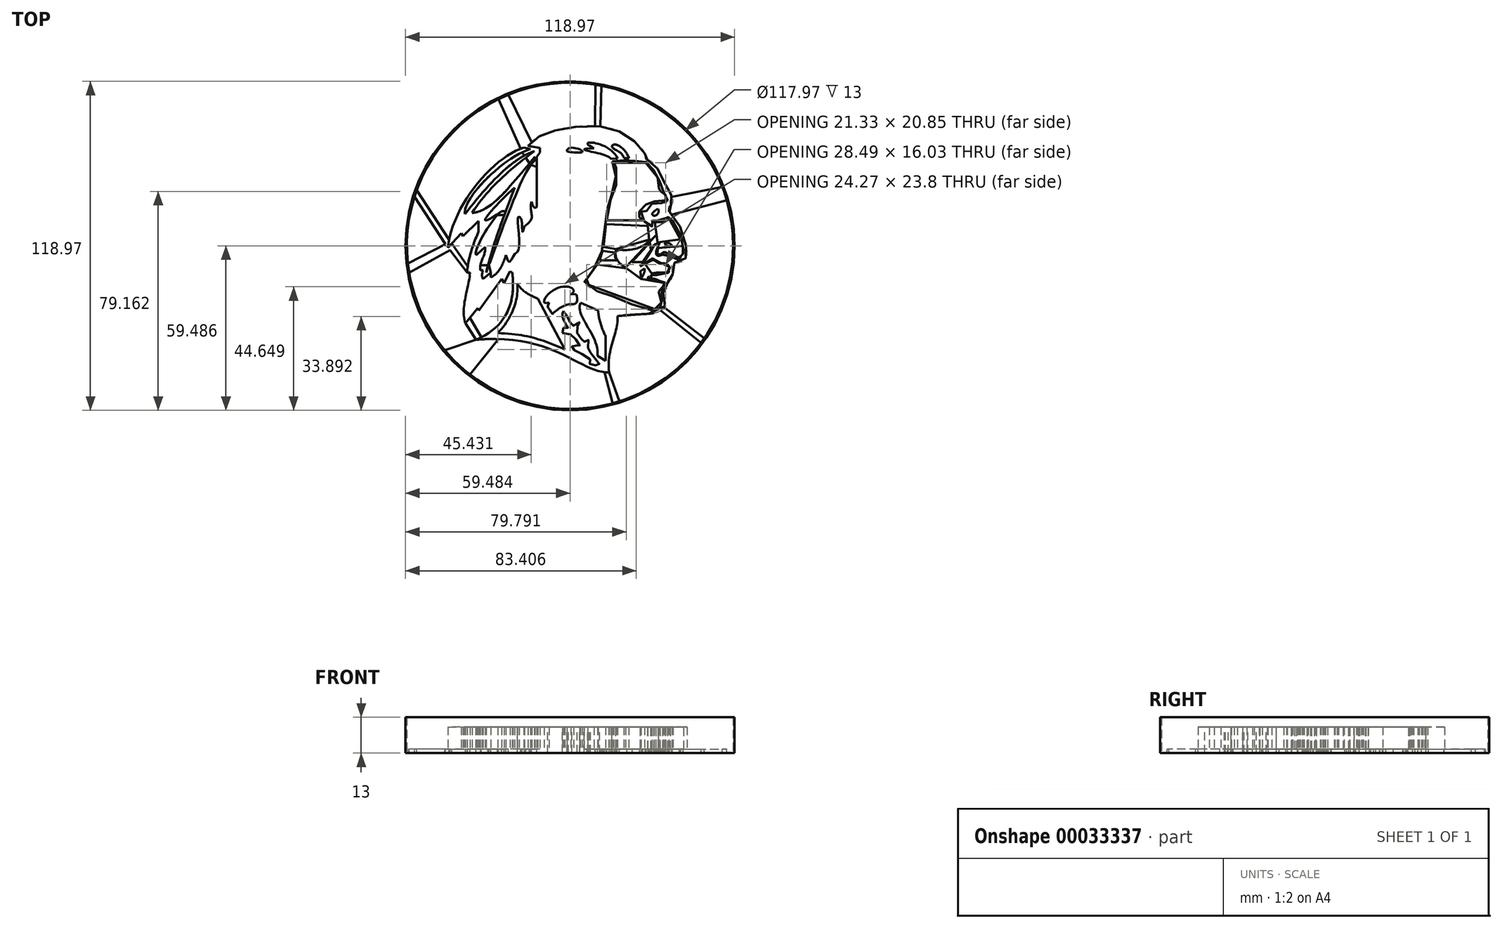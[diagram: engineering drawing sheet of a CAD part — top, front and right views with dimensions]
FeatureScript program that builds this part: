
annotation { "Feature Type Name" : "Feature", "Feature Type Description" : "" }
export const myFeature = defineFeature(function(context is Context, id is Id, definition is map)
    precondition{}
    {
        {
            var Q0;
            Q0=qCreatedBy(makeId("Top.planeOp"),FACE);
            var sketch = newSketch(context, id + "F0", { "sketchPlane" : qUnion([Q0])});
            skCircle(sketch, "E0", {"center": v(7.53, 11.46) * mm, "radius": 59.49 * mm});
            skPoint(sketch, "E0.first.point", {"position": v(-51.93, 13.03) * mm});
            skPoint(sketch, "E0.second.point", {"position": v(66.92, 7.92) * mm});
            skPoint(sketch, "E0.third.point", {"position": v(5.79, 70.92) * mm});
            skSolve(sketch);
        }
        {
            var Q0;
            Q0=makeQuery(id+"F0.imprint","IMPRINT",FACE,{"disambiguationData":[TD([[makeQuery(id+"F0.imprint","IMPRINT",EDGE,{"derivedFrom":sQuery(id+"F0.wireOp",EDGE,"E0")}),1.0]])]});
            extrude(context, id + "F1", {"entities" : qUnion([Q0]), "depth" : 12 * mm});
        }
        {
            var Q0;
            Q0=makeQuery(id+"F1.opExtrude","CAP_FACE",FACE,{"disambiguationData":[OSD([sQuery(id+"F0.wireOp",EDGE,"E0")])],"isStart":false});
            shell(context, id + "F2", {"entities" : qUnion([Q0]), "thickness" : .5 * mm});
        }
        {
            var Q0;
            {var subQ0=sQuery(id+"F0.wireOp",EDGE,"E0");Q0=makeQuery(id+"F2.opShell","OFFSET_FACE",FACE,{"disambiguationData":[OSD([subQ0]),TDD([makeQuery(id+"F1.opExtrude","CAP_FACE",FACE,{"disambiguationData":[OSD([subQ0])],"isStart":true})])]});}
            var sketch = newSketch(context, id + "F3", { "sketchPlane" : qUnion([Q0])});
            skFitSpline(sketch, "E1", {"points": [v(-9.15, 46.95) * mm, v(-36.63, 10.74) * mm], "startDerivative": vector(-33.15, -9.52) * mm, "endDerivative": vector(-3.72, -44.42) * mm});
            skFitSpline(sketch, "E2", {"points": [v(-36.63, 10.74) * mm, v(-31.8, 15.95) * mm], "startDerivative": vector(4.82, 5.2) * mm, "endDerivative": vector(4.82, 5.2) * mm});
            skFitSpline(sketch, "E3", {"points": [v(-31.8, 15.95) * mm, v(-31.11, 14.95) * mm], "startDerivative": vector(0.69, -1) * mm, "endDerivative": vector(0.69, -1) * mm});
            skFitSpline(sketch, "E4", {"points": [v(-5.09, 42.36) * mm, v(-5.09, 43.66) * mm], "startDerivative": vector(0, 1.3) * mm, "endDerivative": vector(0, 1.3) * mm});
            skFitSpline(sketch, "E5", {"points": [v(-5.09, 43.66) * mm, v(-27.88, 23.37) * mm], "startDerivative": vector(-23.04, -26.12) * mm, "endDerivative": vector(-22.32, -0.88) * mm});
            skFitSpline(sketch, "E6", {"points": [v(-27.88, 23.37) * mm, v(-5.34, 45.7) * mm], "startDerivative": vector(17.84, 27.64) * mm, "endDerivative": vector(23.73, 17.5) * mm});
            skFitSpline(sketch, "E7", {"points": [v(-5.34, 45.7) * mm, v(-30.47, 22.94) * mm], "startDerivative": vector(-25.9, -8.68) * mm, "endDerivative": vector(-24.74, -31.1) * mm});
            skFitSpline(sketch, "E8", {"points": [v(-30.47, 22.94) * mm, v(-6.79, 46.48) * mm], "startDerivative": vector(-3.33, 15.62) * mm, "endDerivative": vector(31.1, 9.84) * mm});
            skFitSpline(sketch, "E9", {"points": [v(-6.79, 46.48) * mm, v(-9.15, 46.95) * mm], "startDerivative": vector(-2.36, 0.47) * mm, "endDerivative": vector(-2.36, 0.47) * mm});
            skFitSpline(sketch, "E10", {"points": [v(-31.11, 14.95) * mm, v(-25.52, 20.45) * mm], "startDerivative": vector(5.6, 5.5) * mm, "endDerivative": vector(5.6, 5.5) * mm});
            skFitSpline(sketch, "E11", {"points": [v(-25.52, 20.45) * mm, v(-25.52, 16.55) * mm], "startDerivative": vector(0, -3.9) * mm, "endDerivative": vector(0, -3.9) * mm});
            skFitSpline(sketch, "E12", {"points": [v(-25.52, 16.55) * mm, v(-29.7, 1.74) * mm], "startDerivative": vector(-6.96, -15.11) * mm, "endDerivative": vector(-0.88, -13.52) * mm});
            skFitSpline(sketch, "E13", {"points": [v(-29.7, 1.74) * mm, v(-28.61, 1.74) * mm], "startDerivative": vector(1.09, 0) * mm, "endDerivative": vector(1.09, 0) * mm});
            skFitSpline(sketch, "E14", {"points": [v(-28.61, 1.74) * mm, v(-30.24, -16.6) * mm], "startDerivative": vector(-1.62, -18.33) * mm, "endDerivative": vector(6.1, -16.78) * mm});
            skFitSpline(sketch, "E15", {"points": [v(-30.24, -16.6) * mm, v(-25.84, -11.03) * mm], "startDerivative": vector(4.4, 5.57) * mm, "endDerivative": vector(4.4, 5.57) * mm});
            skFitSpline(sketch, "E16", {"points": [v(-25.84, -11.03) * mm, v(-25.44, -12) * mm], "startDerivative": vector(0.4, -0.96) * mm, "endDerivative": vector(0.4, -0.96) * mm});
            skFitSpline(sketch, "E17", {"points": [v(-25.44, -12) * mm, v(-17.17, -0.55) * mm], "startDerivative": vector(8.27, 11.44) * mm, "endDerivative": vector(8.27, 11.44) * mm});
            skFitSpline(sketch, "E18", {"points": [v(-17.17, -0.55) * mm, v(-16.27, -1.99) * mm], "startDerivative": vector(0.9, -1.44) * mm, "endDerivative": vector(0.9, -1.44) * mm});
            skFitSpline(sketch, "E19", {"points": [v(-16.27, -1.99) * mm, v(-14.18, 2.32) * mm], "startDerivative": vector(2.1, 4.3) * mm, "endDerivative": vector(2.1, 4.3) * mm});
            skFitSpline(sketch, "E20", {"points": [v(-14.18, 2.32) * mm, v(-13.39, 1.7) * mm], "startDerivative": vector(0.8, -0.62) * mm, "endDerivative": vector(0.8, -0.62) * mm});
            skFitSpline(sketch, "E21", {"points": [v(-13.39, 1.7) * mm, v(-26.5, -22.52) * mm], "startDerivative": vector(3.2, -23.1) * mm, "endDerivative": vector(-39.4, -16.16) * mm});
            skFitSpline(sketch, "E22", {"points": [v(-26.5, -22.52) * mm, v(21.64, -34.31) * mm], "startDerivative": vector(86.82, 7.34) * mm, "endDerivative": vector(31.4, 1.39) * mm});
            skFitSpline(sketch, "E23", {"points": [v(21.64, -34.31) * mm, v(24.69, -14) * mm], "startDerivative": vector(-2.89, 25.9) * mm, "endDerivative": vector(-2.05, 15.2) * mm});
            skFitSpline(sketch, "E24", {"points": [v(24.69, -14) * mm, v(39.93, -12.2) * mm, v(42.05, -8.84) * mm, v(41.21, -5.53) * mm, v(42.66, -3.65) * mm, v(43.16, -0.9) * mm, v(44.42, -0.49) * mm, v(44.42, 5.18) * mm, v(45.19, 5.3) * mm, v(48.22, 5.86) * mm, v(49.79, 8.1) * mm, v(49.5, 11.54) * mm, v(46.75, 19.39) * mm, v(43.4, 23.85) * mm, v(43.33, 24.4) * mm, v(43.73, 26.1) * mm, v(44.36, 26.48) * mm, v(44.66, 28.5) * mm, v(42.08, 33.4) * mm, v(40.66, 36.42) * mm, v(38.63, 40.1) * mm, v(35.68, 42.55) * mm, v(35.22, 42.59) * mm, v(35.02, 43.17) * mm, v(34.4, 45.2) * mm, v(31.33, 48.76) * mm, v(26.07, 52.42) * mm, v(18.52, 54.63) * mm, v(7.38, 54.25) * mm, v(0.41, 52.69) * mm, v(-4.75, 50.41) * mm, v(-7.71, 47.66) * mm], "startDerivative": vector(305.64, 45.18) * mm, "endDerivative": vector(-76.3, -84.2) * mm});
            skFitSpline(sketch, "E25", {"points": [v(-7.71, 47.66) * mm, v(-3.36, 46.9) * mm], "startDerivative": vector(4.35, -0.77) * mm, "endDerivative": vector(4.35, -0.77) * mm});
            skFitSpline(sketch, "E26", {"points": [v(-3.36, 46.9) * mm, v(-3.36, 45.21) * mm], "startDerivative": vector(0, -1.68) * mm, "endDerivative": vector(0, -1.68) * mm});
            skFitSpline(sketch, "E27", {"points": [v(-3.36, 45.21) * mm, v(-4.46, 43.68) * mm], "startDerivative": vector(-1.1, -1.53) * mm, "endDerivative": vector(-1.1, -1.53) * mm});
            skFitSpline(sketch, "E28", {"points": [v(-4.46, 43.68) * mm, v(-4.46, 25.48) * mm], "startDerivative": vector(0, -18.2) * mm, "endDerivative": vector(0, -18.2) * mm});
            skFitSpline(sketch, "E29", {"points": [v(-4.46, 25.48) * mm, v(-6.37, 27.36) * mm], "startDerivative": vector(-2.7, -1.39) * mm, "endDerivative": vector(-1.92, 7.05) * mm});
            skFitSpline(sketch, "E30", {"points": [v(-6.37, 27.36) * mm, v(-6.37, 21.44) * mm, v(-8.9, 18.53) * mm], "startDerivative": vector(-4.08, -13.4) * mm, "endDerivative": vector(-6.92, -5.6) * mm});
            skFitSpline(sketch, "E31", {"points": [v(-8.9, 18.53) * mm, v(-9.67, 16.48) * mm, v(-10.03, 20.82) * mm, v(-11, 21.93) * mm, v(-11.43, 20.6) * mm, v(-10.99, 10.19) * mm, v(-12.7, 8.17) * mm, v(-14.41, 5.61) * mm, v(-15.63, 8.07) * mm], "startDerivative": vector(-9.44, -31.77) * mm, "endDerivative": vector(-9.92, 32.78) * mm});
            skFitSpline(sketch, "E32", {"points": [v(-15.63, 8.07) * mm, v(-21.11, 0) * mm], "startDerivative": vector(-3.75, -12.02) * mm, "endDerivative": vector(-7.77, -3.86) * mm});
            skFitSpline(sketch, "E33", {"points": [v(-21.11, 0) * mm, v(-21.11, 1.8) * mm], "startDerivative": vector(0, 1.8) * mm, "endDerivative": vector(0, 1.8) * mm});
            skFitSpline(sketch, "E34", {"points": [v(-21.11, 1.8) * mm, v(-23.96, -0.53) * mm], "startDerivative": vector(-2.85, -2.33) * mm, "endDerivative": vector(-2.85, -2.33) * mm});
            skFitSpline(sketch, "E35", {"points": [v(-23.96, -0.53) * mm, v(-23.96, 2.67) * mm], "startDerivative": vector(-1.2, 1.6) * mm, "endDerivative": vector(1.41, 4.07) * mm});
            skFitSpline(sketch, "E36", {"points": [v(-23.96, 2.67) * mm, v(-24.9, 2.67) * mm], "startDerivative": vector(-0.94, 0) * mm, "endDerivative": vector(-0.94, 0) * mm});
            skFitSpline(sketch, "E37", {"points": [v(-24.9, 2.67) * mm, v(-23.15, 11.01) * mm], "startDerivative": vector(-1.4, 8.6) * mm, "endDerivative": vector(-1.04, 8.36) * mm});
            skFitSpline(sketch, "E38", {"points": [v(-23.15, 11.01) * mm, v(-26.14, 8.3) * mm], "startDerivative": vector(-3, -2.7) * mm, "endDerivative": vector(-3, -2.7) * mm});
            skFitSpline(sketch, "E39", {"points": [v(-26.14, 8.3) * mm, v(-17.24, 24) * mm], "startDerivative": vector(-6.04, -1.8) * mm, "endDerivative": vector(16.01, 13.76) * mm});
            skFitSpline(sketch, "E40", {"points": [v(-17.24, 24) * mm, v(-12.45, 32.51) * mm], "startDerivative": vector(-44.66, -32.02) * mm, "endDerivative": vector(6.2, 4.22) * mm});
            skFitSpline(sketch, "E41", {"points": [v(-12.45, 32.51) * mm, v(-22.84, 1.74) * mm], "startDerivative": vector(-12.12, -31.5) * mm, "endDerivative": vector(-7.38, -30.43) * mm});
            skFitSpline(sketch, "E42", {"points": [v(-22.84, 1.74) * mm, v(-5.09, 42.36) * mm], "startDerivative": vector(16.99, 44.79) * mm, "endDerivative": vector(12.56, 7.44) * mm});
            skFitSpline(sketch, "E43", {"points": [v(12.05, 45.52) * mm, v(7.29, 45.42) * mm, v(6.43, 45.97) * mm, v(8.14, 46.93) * mm, v(12.05, 45.52) * mm]});
            skFitSpline(sketch, "E44", {"points": [v(16.2, 46.76) * mm, v(22.31, 42.96) * mm], "startDerivative": vector(-30.9, -1.52) * mm, "endDerivative": vector(4.22, -7.27) * mm});
            skFitSpline(sketch, "E45", {"points": [v(27, 43.12) * mm, v(28.81, 43.11) * mm], "startDerivative": vector(1.8, 0) * mm, "endDerivative": vector(1.8, 0) * mm});
            skFitSpline(sketch, "E46", {"points": [v(28.81, 43.11) * mm, v(23.37, 48.1) * mm], "startDerivative": vector(-1.96, 7.28) * mm, "endDerivative": vector(-5.93, -0.5) * mm});
            skFitSpline(sketch, "E47", {"points": [v(23.37, 48.1) * mm, v(27, 43.12) * mm], "startDerivative": vector(-8.2, -4.56) * mm, "endDerivative": vector(1.09, -9.1) * mm});
            skFitSpline(sketch, "E48", {"points": [v(22.77, 42) * mm, v(24.02, 38.9) * mm, v(23, 30.55) * mm, v(22.05, 28.83) * mm, v(20.78, 23.25) * mm, v(19.76, 14.45) * mm, v(17.96, 6.24) * mm, v(14.46, 1.05) * mm, v(12.8, -1.85) * mm, v(16.95, -4.86) * mm, v(22.21, -6.53) * mm, v(27.8, -8.95) * mm, v(36.7, -11.8) * mm, v(38.2, -11.94) * mm, v(39.57, -11.43) * mm, v(40.86, -10.04) * mm, v(40.9, -7.95) * mm, v(40.26, -5.58) * mm, v(40.28, -5.02) * mm, v(41.6, -3.23) * mm, v(42.08, -1.93) * mm, v(41.24, -1.74) * mm, v(37.72, -0.43) * mm, v(35.64, -0.43) * mm, v(35.72, 0) * mm, v(37.52, 1.28) * mm, v(37.92, 1.44) * mm, v(38.3, 1.19) * mm, v(38.9, 0.82) * mm, v(40.5, 1.38) * mm, v(43.37, 1.72) * mm, v(43.83, 2.46) * mm, v(43.67, 3.48) * mm, v(42.02, 5.29) * mm, v(39.93, 5.31) * mm, v(37.95, 6.65) * mm, v(37.48, 6.85) * mm, v(37.08, 6.7) * mm, v(32.87, 4.05) * mm], "startDerivative": vector(53.72, -79.37) * mm, "endDerivative": vector(-145.32, -92.55) * mm});
            skFitSpline(sketch, "E49", {"points": [v(32.87, 4.05) * mm, v(37.87, 11.85) * mm], "startDerivative": vector(6.86, 7.68) * mm, "endDerivative": vector(2.48, 7.9) * mm});
            skFitSpline(sketch, "E50", {"points": [v(37.87, 11.85) * mm, v(39.97, 12.6) * mm], "startDerivative": vector(2.17, 0.47) * mm, "endDerivative": vector(2.1, 0.75) * mm});
            skFitSpline(sketch, "E51", {"points": [v(39.97, 12.6) * mm, v(41.1, 8.23) * mm], "startDerivative": vector(-3.77, -8.3) * mm, "endDerivative": vector(11.52, 4.15) * mm});
            skFitSpline(sketch, "E52", {"points": [v(41.1, 8.23) * mm, v(41.86, 8.62) * mm, v(42.96, 8.23) * mm, v(44.51, 7.28) * mm, v(45.65, 6.6) * mm, v(46.69, 6.46) * mm, v(47.87, 7.03) * mm, v(48.63, 8.23) * mm, v(48.52, 10.96) * mm, v(47.22, 16.12) * mm, v(44.96, 20.18) * mm, v(43.24, 21.99) * mm, v(42.96, 22.17) * mm, v(42.6, 21.75) * mm, v(41.44, 20.79) * mm, v(39.83, 20.61) * mm, v(39.44, 20.67) * mm, v(39.6, 20.22) * mm, v(37.61, 20.59) * mm, v(37.3, 20.55) * mm, v(37.31, 20.21) * mm, v(37.82, 19.5) * mm, v(37.8, 19) * mm, v(36.65, 18.25) * mm, v(36.09, 18.45) * mm, v(34.51, 20.12) * mm, v(33.03, 22.68) * mm, v(33.08, 23.53) * mm, v(33.76, 24.06) * mm, v(34.4, 24.16) * mm, v(34.68, 23.83) * mm, v(35.35, 24.16) * mm, v(36.07, 25.01) * mm, v(36.7, 25.45) * mm, v(36.68, 25.61) * mm, v(35.87, 25.8) * mm, v(35.9, 26.22) * mm, v(36.75, 26.32) * mm, v(37.2, 26.6) * mm, v(38.58, 27.25) * mm, v(40.25, 27.04) * mm, v(41.4, 26.62) * mm, v(42.43, 26.85) * mm, v(42.85, 27.98) * mm, v(42.8, 29.21) * mm, v(41.7, 30.82) * mm, v(40.53, 31.68) * mm, v(39.96, 34.35) * mm, v(39.26, 36.62) * mm, v(37.44, 39.18) * mm, v(36.38, 40.67) * mm, v(34.92, 41.78) * mm, v(32.2, 41.95) * mm, v(31.04, 42.13) * mm, v(29.01, 42.2) * mm, v(27.4, 42.37) * mm, v(25.34, 42.35) * mm, v(22.77, 42) * mm], "startDerivative": vector(51.42, 38.87) * mm, "endDerivative": vector(-106.33, -16.92) * mm});
            skFitSpline(sketch, "E53", {"points": [v(16.2, 46.76) * mm, v(24.71, 43.06) * mm], "startDerivative": vector(-22.76, 10.16) * mm, "endDerivative": vector(8.73, -19.57) * mm});
            skFitSpline(sketch, "E54", {"points": [v(24.71, 43.06) * mm, v(22.31, 42.96) * mm], "startDerivative": vector(-2.4, -0.1) * mm, "endDerivative": vector(-2.4, -0.1) * mm});
            skFitSpline(sketch, "E55", {"points": [v(38.58, 15.26) * mm, v(24.23, 10.1) * mm], "startDerivative": vector(-13.9, -13.92) * mm, "endDerivative": vector(-19.24, 2.1) * mm});
            skFitSpline(sketch, "E56", {"points": [v(24.23, 10.1) * mm, v(27.6, 3.65) * mm], "startDerivative": vector(-3.71, -11.3) * mm, "endDerivative": vector(2.74, -1.3) * mm});
            skFitSpline(sketch, "E57", {"points": [v(27.6, 3.65) * mm, v(38.58, 15.26) * mm], "startDerivative": vector(10.98, 11.6) * mm, "endDerivative": vector(10.98, 11.6) * mm});
            skFitSpline(sketch, "E58", {"points": [v(34.44, 3.25) * mm, v(32.92, 2.22) * mm], "startDerivative": vector(-1.52, -1.03) * mm, "endDerivative": vector(-1.52, -1.03) * mm});
            skFitSpline(sketch, "E59", {"points": [v(32.92, 2.22) * mm, v(33.18, -0.23) * mm], "startDerivative": vector(0.25, -2.44) * mm, "endDerivative": vector(0.25, -2.44) * mm});
            skFitSpline(sketch, "E60", {"points": [v(33.18, -0.23) * mm, v(34.44, 3.25) * mm], "startDerivative": vector(2.3, 2.04) * mm, "endDerivative": vector(-0.83, 3.64) * mm});
            skFitSpline(sketch, "E61", {"points": [v(41.6, 12.58) * mm, v(42.8, 11.4) * mm, v(44.44, 11.52) * mm], "startDerivative": vector(2.14, -3) * mm, "endDerivative": vector(3.52, 0.88) * mm});
            skFitSpline(sketch, "E62", {"points": [v(44.44, 11.52) * mm, v(41.6, 12.58) * mm], "startDerivative": vector(-0.58, 1.08) * mm, "endDerivative": vector(-4.54, -0.7) * mm});
            skFitSpline(sketch, "E63", {"points": [v(39.34, 24.81) * mm, v(37.18, 23.06) * mm], "startDerivative": vector(-2.94, -1.27) * mm, "endDerivative": vector(-1.66, -1.96) * mm});
            skFitSpline(sketch, "E64", {"points": [v(37.18, 23.06) * mm, v(37.95, 22.27) * mm, v(39.52, 23.42) * mm, v(39.34, 24.81) * mm], "startDerivative": vector(2.06, -4) * mm, "endDerivative": vector(-1.81, 4.2) * mm});
            skFitSpline(sketch, "E65", {"points": [v(5.62, -26.04) * mm, v(-4.17, -7.65) * mm], "startDerivative": vector(-9.78, 18.39) * mm, "endDerivative": vector(-9.78, 18.39) * mm});
            skFitSpline(sketch, "E66", {"points": [v(-4.17, -7.65) * mm, v(-11.58, -2.24) * mm], "startDerivative": vector(-6.61, 3.26) * mm, "endDerivative": vector(-7.29, 10.64) * mm});
            skFitSpline(sketch, "E67", {"points": [v(-11.58, -2.24) * mm, v(-18.65, -20.12) * mm], "startDerivative": vector(2.01, -15.17) * mm, "endDerivative": vector(-16.38, -16.45) * mm});
            skFitSpline(sketch, "E68", {"points": [v(-18.65, -20.12) * mm, v(5.62, -26.04) * mm], "startDerivative": vector(31.26, -0.68) * mm, "endDerivative": vector(22.67, -10.11) * mm});
            skFitSpline(sketch, "E69", {"points": [v(11.35, -9.15) * mm, v(17.73, -11.9) * mm], "startDerivative": vector(6.38, -2.76) * mm, "endDerivative": vector(6.38, -2.76) * mm});
            skFitSpline(sketch, "E70", {"points": [v(17.73, -11.9) * mm, v(20.35, -21.18) * mm], "startDerivative": vector(0.1, -9.8) * mm, "endDerivative": vector(3.25, -6.64) * mm});
            skFitSpline(sketch, "E71", {"points": [v(20.35, -21.18) * mm, v(20.35, -30.17) * mm], "startDerivative": vector(0, -9) * mm, "endDerivative": vector(0, -9) * mm});
            skFitSpline(sketch, "E72", {"points": [v(20.35, -30.17) * mm, v(17.48, -28.39) * mm], "startDerivative": vector(-2.87, 1.78) * mm, "endDerivative": vector(-2.87, 1.78) * mm});
            skFitSpline(sketch, "E73", {"points": [v(17.48, -28.39) * mm, v(11.35, -9.15) * mm], "startDerivative": vector(2.06, 23.36) * mm, "endDerivative": vector(6.67, 14.81) * mm});
            skFitSpline(sketch, "E74", {"points": [v(0, -9.06) * mm, v(3.2, -3.73) * mm, v(7.87, -6.13) * mm], "startDerivative": vector(-23.87, -7.6) * mm, "endDerivative": vector(-17.62, -12.06) * mm});
            skFitSpline(sketch, "E75", {"points": [v(0, -9.06) * mm, v(-0.5, -10.53) * mm, v(0, -11.45) * mm, v(0.95, -13) * mm, v(1.2, -13.24) * mm, v(1.46, -12.93) * mm, v(4.94, -10.46) * mm, v(7.65, -9.67) * mm, v(9.2, -9.62) * mm, v(10, -8.8) * mm, v(10.13, -7.42) * mm, v(9.76, -6.2) * mm, v(7.87, -6.13) * mm], "startDerivative": vector(-9.3, -18.83) * mm, "endDerivative": vector(-24.1, -3.27) * mm});
            skFitSpline(sketch, "E76", {"points": [v(5.15, -12.23) * mm, v(4.8, -14.56) * mm], "startDerivative": vector(-1.66, -2.16) * mm, "endDerivative": vector(-0.35, -2.33) * mm});
            skLineSegment(sketch, "E77", {"start": v(5.16, -18.17) * mm, "end": v(4.8, -20.08) * mm});
            skFitSpline(sketch, "E78", {"points": [v(4.8, -14.56) * mm, v(6.58, -17.76) * mm, v(6.86, -18.15) * mm, v(6.47, -18.22) * mm, v(5.16, -18.17) * mm], "startDerivative": vector(4.5, -9.02) * mm, "endDerivative": vector(-5.43, 0.3) * mm});
            skFitSpline(sketch, "E79", {"points": [v(4.8, -20.08) * mm, v(7.4, -20.5) * mm, v(8.48, -21.14) * mm, v(9.97, -22.86) * mm, v(11, -24.44) * mm, v(11.03, -24.72) * mm, v(10.18, -24.78) * mm, v(9.44, -24.53) * mm, v(8.32, -24.54) * mm, v(8.25, -25.12) * mm, v(8.52, -26.11) * mm, v(9.1, -26.3) * mm, v(11.26, -27.24) * mm, v(14.56, -29.5) * mm, v(14.87, -29.8) * mm, v(14.9, -30.32) * mm, v(14.69, -31.58) * mm, v(14.88, -31.82) * mm, v(17.89, -31.75) * mm, v(18.22, -31.67) * mm, v(18.05, -31.1) * mm, v(14.09, -26.14) * mm, v(13.93, -25.9) * mm, v(14.03, -25.38) * mm, v(14.16, -22.84) * mm, v(14.03, -22.42) * mm, v(13.67, -22.58) * mm, v(12.5, -23.32) * mm, v(12.2, -23.18) * mm, v(11.71, -22.31) * mm, v(10.36, -20.87) * mm, v(10.06, -19.29) * mm, v(10.28, -17.57) * mm, v(10.98, -16.7) * mm, v(11, -16.27) * mm, v(10.42, -16.38) * mm, v(8.46, -17.57) * mm, v(8, -17.62) * mm, v(7.23, -15.48) * mm, v(6.46, -14.04) * mm, v(6.43, -13.4) * mm, v(5.15, -12.23) * mm], "startDerivative": vector(79.68, -9.23) * mm, "endDerivative": vector(-58.5, 41.16) * mm});
            skSolve(sketch);
        }
        {
            var Q0;
            Q0=makeQuery(id+"F3.imprint","IMPRINT",FACE,{"disambiguationData":[TD([[makeQuery(id+"F3.imprint","IMPRINT",EDGE,{"derivedFrom":sQuery(id+"F3.wireOp",EDGE,"E1")}),1.0]])]});
            var Q1;
            Q1=makeQuery(id+"F3.imprint","IMPRINT",FACE,{"disambiguationData":[TD([[makeQuery(id+"F3.imprint","IMPRINT",EDGE,{"derivedFrom":sQuery(id+"F3.wireOp",EDGE,"E55")}),1.0]])]});
            var Q2;
            Q2=makeQuery(id+"F3.imprint","IMPRINT",FACE,{"disambiguationData":[TD([[makeQuery(id+"F3.imprint","IMPRINT",EDGE,{"derivedFrom":sQuery(id+"F3.wireOp",EDGE,"E61")}),1.0]])]});
            extrude(context, id + "F4", {"entities" : qUnion([Q0, Q1, Q2]), "operationType" : NewBodyOperationType.ADD, "depth" : 8 * mm});
        }
        {
            var Q0;
            Q0=makeQuery(id+"F1.opExtrude","CAP_FACE",FACE,{"disambiguationData":[OSD([sQuery(id+"F0.wireOp",EDGE,"E0")])],"isStart":true});
            extrude(context, id + "F5", {"entities" : qUnion([Q0]), "operationType" : NewBodyOperationType.ADD, "depth" : 1 * mm});
        }
        {
            var Q0;
            {var subQ0=sQuery(id+"F0.wireOp",EDGE,"E0");Q0=makeQuery(id+"F4.boolean.opBoolean","SPLIT",FACE,{"disambiguationData":[TD([makeQuery(id+"F4.opExtrude","SWEPT_FACE",FACE,{"disambiguationData":[OSD([sQuery(id+"F3.wireOp",EDGE,"E1")])]})])],"derivedFrom":makeQuery(id+"F2.opShell","OFFSET_FACE",FACE,{"disambiguationData":[OSD([subQ0]),TDD([makeQuery(id+"F1.opExtrude","CAP_FACE",FACE,{"disambiguationData":[OSD([subQ0])],"isStart":true})])]})});}
            var sketch = newSketch(context, id + "F6", { "sketchPlane" : qUnion([Q0])});
            skLineSegment(sketch, "E80", {"start": v(-18.36, -22.27) * mm, "end": v(-28.64, -35.13) * mm});
            skLineSegment(sketch, "E81", {"start": v(-26.5, -22.52) * mm, "end": v(-37.73, -26.37) * mm});
            skLineSegment(sketch, "E82", {"start": v(-30.24, -16.6) * mm, "end": v(-26.5, -22.52) * mm});
            skLineSegment(sketch, "E83", {"start": v(-28.66, -14.6) * mm, "end": v(-24.59, -21.65) * mm});
            skLineSegment(sketch, "E84", {"start": v(-36.63, 10.74) * mm, "end": v(-29.7, 1.74) * mm});
            skLineSegment(sketch, "E85", {"start": v(-35.24, 12.24) * mm, "end": v(-29.46, 3.99) * mm});
            skLineSegment(sketch, "E86", {"start": v(-36.63, 10.74) * mm, "end": v(-48.73, 29.18) * mm});
            skLineSegment(sketch, "E87", {"start": v(-36.2, 13.7) * mm, "end": v(-47.93, 31.55) * mm});
            skLineSegment(sketch, "E88", {"start": v(-35.92, 9.83) * mm, "end": v(-50.66, 1.8) * mm});
            skLineSegment(sketch, "E89", {"start": v(-37.51, 12.1) * mm, "end": v(-51.1, 5) * mm});
            skLineSegment(sketch, "E90", {"start": v(-51.1, 5) * mm, "end": v(-50.51, 5.07) * mm});
            skLineSegment(sketch, "E91", {"start": v(21.64, -34.31) * mm, "end": v(25.3, -44.8) * mm});
            skLineSegment(sketch, "E92", {"start": v(40.35, -11.97) * mm, "end": v(54.94, -23.65) * mm});
            skLineSegment(sketch, "E93", {"start": v(41.57, -10.78) * mm, "end": v(56.08, -22.05) * mm});
            skLineSegment(sketch, "E94", {"start": v(-22.15, 4.47) * mm, "end": v(-24.85, 4.47) * mm});
            skLineSegment(sketch, "E95", {"start": v(-21.82, 4.45) * mm, "end": v(-21.11, 1.8) * mm});
            skLineSegment(sketch, "E96", {"start": v(-18.76, 22.52) * mm, "end": v(-16.24, 22.52) * mm});
            skLineSegment(sketch, "E97", {"start": v(-17.24, 24) * mm, "end": v(-15.7, 24) * mm});
            skLineSegment(sketch, "E98", {"start": v(-4.46, 40.03) * mm, "end": v(-6.67, 40.73) * mm});
            skLineSegment(sketch, "E99", {"start": v(-7.13, 41.29) * mm, "end": v(-8.5, 43.32) * mm});
            skLineSegment(sketch, "E100", {"start": v(-8.91, 44.13) * mm, "end": v(-9.86, 45.23) * mm});
            skLineSegment(sketch, "E101", {"start": v(-9.15, 46.95) * mm, "end": v(-7.71, 47.66) * mm});
            skLineSegment(sketch, "E102", {"start": v(-10.4, 46.53) * mm, "end": v(-18.32, 64.47) * mm});
            skLineSegment(sketch, "E103", {"start": v(-6.44, 49) * mm, "end": v(-14.73, 66.08) * mm});
            skLineSegment(sketch, "E104", {"start": v(16.54, 54.78) * mm, "end": v(16.78, 69.71) * mm});
            skLineSegment(sketch, "E105", {"start": v(16.78, 69.71) * mm, "end": v(16.71, 69.23) * mm});
            skLineSegment(sketch, "E106", {"start": v(44.46, 29.17) * mm, "end": v(62.57, 32.68) * mm});
            skLineSegment(sketch, "E107", {"start": v(44.28, 22.72) * mm, "end": v(64.2, 27.85) * mm});
            skLineSegment(sketch, "E108", {"start": v(34.27, 4.94) * mm, "end": v(36.98, 1.01) * mm});
            skLineSegment(sketch, "E109", {"start": v(33.98, 5.26) * mm, "end": v(17.24, 6.03) * mm});
            skLineSegment(sketch, "E110", {"start": v(20.02, -34.26) * mm, "end": v(22.99, -45.47) * mm});
            skLineSegment(sketch, "E111", {"start": v(22.99, -45.47) * mm, "end": v(22.88, -45.13) * mm});
            skLineSegment(sketch, "E112", {"start": v(18.93, 70.54) * mm, "end": v(18.36, 52.47) * mm});
            skLineSegment(sketch, "E113", {"start": v(16.52, 4.82) * mm, "end": v(27.36, 4.35) * mm});
            skLineSegment(sketch, "E114", {"start": v(27.36, 4.35) * mm, "end": v(33.2, -0.21) * mm});
            skLineSegment(sketch, "E115", {"start": v(33.2, -0.21) * mm, "end": v(36.57, -0.21) * mm});
            skLineSegment(sketch, "E116", {"start": v(36.25, 19.55) * mm, "end": v(19.31, 19.55) * mm});
            skLineSegment(sketch, "E117", {"start": v(19.28, 20.44) * mm, "end": v(35.07, 20.44) * mm});
            skLineSegment(sketch, "E118", {"start": v(35.8, 19.16) * mm, "end": v(37.1, 8.64) * mm});
            skLineSegment(sketch, "E119", {"start": v(39.24, 11.64) * mm, "end": v(37.59, 19.3) * mm});
            skLineSegment(sketch, "E120", {"start": v(39.6, 12.47) * mm, "end": v(48.14, 13.55) * mm});
            skLineSegment(sketch, "E121", {"start": v(48.9, 11.54) * mm, "end": v(38.9, 10.97) * mm});
            skLineSegment(sketch, "E122", {"start": v(24.62, 8.8) * mm, "end": v(18.22, 10.12) * mm});
            skLineSegment(sketch, "E123", {"start": v(18.22, 10.12) * mm, "end": v(18.22, 11.08) * mm});
            skLineSegment(sketch, "E124", {"start": v(18.22, 11.08) * mm, "end": v(25.34, 9.62) * mm});
            skSolve(sketch);
        }
        {
            var Q0;
            {var subQ2=sQuery(id+"F6.wireOp",EDGE,"E87");Q0=makeQuery(id+"F6.imprint","IMPRINT",FACE,{"disambiguationData":[TD([[makeQuery(id+"F6.imprint","IMPRINT",EDGE,{"derivedFrom":subQ2}),-1.0]])]});}
            extrude(context, id + "F7", {"entities" : qUnion([Q0]), "operationType" : NewBodyOperationType.REMOVE, "oppositeDirection" : true, "depth" : 25 * mm});
        }
        {
            var Q0;
            {var subQ2=sQuery(id+"F6.wireOp",EDGE,"E103");Q0=makeQuery(id+"F6.imprint","IMPRINT",FACE,{"disambiguationData":[TD([[makeQuery(id+"F6.imprint","IMPRINT",EDGE,{"derivedFrom":subQ2}),-1.0]])]});}
            var Q1;
            {var subQ1=sQuery(id+"F6.wireOp",EDGE,"E100");Q1=makeQuery(id+"F6.imprint","IMPRINT",FACE,{"disambiguationData":[TD([[makeQuery(id+"F6.imprint","IMPRINT",EDGE,{"derivedFrom":subQ1}),1.0]])]});}
            var Q2;
            {var subQ1=sQuery(id+"F6.wireOp",EDGE,"E99");Q2=makeQuery(id+"F6.imprint","IMPRINT",FACE,{"disambiguationData":[TD([[makeQuery(id+"F6.imprint","IMPRINT",EDGE,{"derivedFrom":subQ1}),1.0]])]});}
            var Q3;
            {var subQ2=sQuery(id+"F6.wireOp",EDGE,"E95");Q3=makeQuery(id+"F6.imprint","IMPRINT",FACE,{"disambiguationData":[TD([[makeQuery(id+"F6.imprint","IMPRINT",EDGE,{"derivedFrom":subQ2}),1.0]])]});}
            var Q4;
            {var subQ1=sQuery(id+"F6.wireOp",EDGE,"E97");Q4=makeQuery(id+"F6.imprint","IMPRINT",FACE,{"disambiguationData":[TD([[makeQuery(id+"F6.imprint","IMPRINT",EDGE,{"derivedFrom":subQ1}),1.0]])]});}
            var Q5;
            {var subQ2=sQuery(id+"F6.wireOp",EDGE,"E94");Q5=makeQuery(id+"F6.imprint","IMPRINT",FACE,{"disambiguationData":[TD([[makeQuery(id+"F6.imprint","IMPRINT",EDGE,{"derivedFrom":subQ2}),-1.0]])]});}
            extrude(context, id + "F8", {"entities" : qUnion([Q0, Q1, Q2, Q3, Q4, Q5]), "operationType" : NewBodyOperationType.REMOVE, "oppositeDirection" : true, "depth" : 25 * mm});
        }
        {
            var Q0;
            {var subQ2=sQuery(id+"F6.wireOp",EDGE,"E93");Q0=makeQuery(id+"F6.imprint","IMPRINT",FACE,{"disambiguationData":[TD([[makeQuery(id+"F6.imprint","IMPRINT",EDGE,{"derivedFrom":subQ2}),1.0]])]});}
            var Q1;
            {var subQ5=sQuery(id+"F6.wireOp",EDGE,"E91");Q1=makeQuery(id+"F6.imprint","IMPRINT",FACE,{"disambiguationData":[TD([[makeQuery(id+"F6.imprint","IMPRINT",EDGE,{"derivedFrom":subQ5}),1.0]])]});}
            var Q2;
            {var subQ2=sQuery(id+"F6.wireOp",EDGE,"E80");Q2=makeQuery(id+"F6.imprint","IMPRINT",FACE,{"disambiguationData":[TD([[makeQuery(id+"F6.imprint","IMPRINT",EDGE,{"derivedFrom":subQ2}),1.0]])]});}
            var Q3;
            {var subQ1=sQuery(id+"F6.wireOp",EDGE,"E83");Q3=makeQuery(id+"F6.imprint","IMPRINT",FACE,{"disambiguationData":[TD([[makeQuery(id+"F6.imprint","IMPRINT",EDGE,{"derivedFrom":subQ1}),1.0]])]});}
            var Q4;
            {var subQ3=sQuery(id+"F6.wireOp",EDGE,"E81");Q4=makeQuery(id+"F6.imprint","IMPRINT",FACE,{"disambiguationData":[TD([[makeQuery(id+"F6.imprint","IMPRINT",EDGE,{"derivedFrom":subQ3}),-1.0]])]});}
            var Q5;
            {var subQ2=sQuery(id+"F6.wireOp",EDGE,"E89");Q5=makeQuery(id+"F6.imprint","IMPRINT",FACE,{"disambiguationData":[TD([[makeQuery(id+"F6.imprint","IMPRINT",EDGE,{"derivedFrom":subQ2}),-1.0]])]});}
            var Q6;
            {var subQ1=sQuery(id+"F6.wireOp",EDGE,"E85");Q6=makeQuery(id+"F6.imprint","IMPRINT",FACE,{"disambiguationData":[TD([[makeQuery(id+"F6.imprint","IMPRINT",EDGE,{"derivedFrom":subQ1}),1.0]])]});}
            extrude(context, id + "F9", {"entities" : qUnion([Q0, Q1, Q2, Q3, Q4, Q5, Q6]), "operationType" : NewBodyOperationType.REMOVE, "oppositeDirection" : true, "depth" : 25 * mm});
        }
        {
            var Q0;
            {var subQ3=sQuery(id+"F6.wireOp",EDGE,"E106");Q0=makeQuery(id+"F6.imprint","IMPRINT",FACE,{"disambiguationData":[TD([[makeQuery(id+"F6.imprint","IMPRINT",EDGE,{"derivedFrom":subQ3}),1.0]])]});}
            extrude(context, id + "F10", {"entities" : qUnion([Q0]), "operationType" : NewBodyOperationType.REMOVE, "oppositeDirection" : true, "depth" : 25 * mm});
        }
        {
            var Q0;
            Q0=makeQuery(id+"F3.imprint","IMPRINT",FACE,{"disambiguationData":[TD([[makeQuery(id+"F3.imprint","IMPRINT",EDGE,{"derivedFrom":sQuery(id+"F3.wireOp",EDGE,"E44")}),1.0]])]});
            var Q1;
            Q1=makeQuery(id+"F3.imprint","IMPRINT",FACE,{"disambiguationData":[TD([[makeQuery(id+"F3.imprint","IMPRINT",EDGE,{"derivedFrom":sQuery(id+"F3.wireOp",EDGE,"E43")}),-1.0]])]});
            var Q2;
            Q2=makeQuery(id+"F3.imprint","IMPRINT",FACE,{"disambiguationData":[TD([[makeQuery(id+"F3.imprint","IMPRINT",EDGE,{"derivedFrom":sQuery(id+"F3.wireOp",EDGE,"E45")}),1.0]])]});
            extrude(context, id + "F11", {"entities" : qUnion([Q0, Q1, Q2]), "operationType" : NewBodyOperationType.REMOVE, "oppositeDirection" : true, "depth" : 25 * mm});
        }
        {
            var Q0;
            Q0=makeQuery(id+"F3.imprint","IMPRINT",FACE,{"disambiguationData":[TD([[makeQuery(id+"F3.imprint","IMPRINT",EDGE,{"derivedFrom":sQuery(id+"F3.wireOp",EDGE,"E58")}),1.0]])]});
            extrude(context, id + "F12", {"entities" : qUnion([Q0]), "operationType" : NewBodyOperationType.ADD, "depth" : 8 * mm});
        }
        {
            var Q0;
            Q0=makeQuery(id+"F3.imprint","IMPRINT",FACE,{"disambiguationData":[TD([[makeQuery(id+"F3.imprint","IMPRINT",EDGE,{"derivedFrom":sQuery(id+"F3.wireOp",EDGE,"E69")}),-1.0]])]});
            var Q1;
            Q1=makeQuery(id+"F3.imprint","IMPRINT",FACE,{"disambiguationData":[TD([[makeQuery(id+"F3.imprint","IMPRINT",EDGE,{"derivedFrom":sQuery(id+"F3.wireOp",EDGE,"E74")}),-1.0]])]});
            var Q2;
            Q2=makeQuery(id+"F3.imprint","IMPRINT",FACE,{"disambiguationData":[TD([[makeQuery(id+"F3.imprint","IMPRINT",EDGE,{"derivedFrom":sQuery(id+"F3.wireOp",EDGE,"E65")}),1.0]])]});
            var Q3;
            Q3=makeQuery(id+"F3.imprint","IMPRINT",FACE,{"disambiguationData":[TD([[makeQuery(id+"F3.imprint","IMPRINT",EDGE,{"derivedFrom":sQuery(id+"F3.wireOp",EDGE,"E76")}),1.0]])]});
            extrude(context, id + "F13", {"entities" : qUnion([Q0, Q1, Q2, Q3]), "operationType" : NewBodyOperationType.REMOVE, "oppositeDirection" : true, "depth" : 25 * mm});
        }
        {
            var Q0;
            Q0=makeQuery(id+"F3.imprint","IMPRINT",FACE,{"disambiguationData":[TD([[makeQuery(id+"F3.imprint","IMPRINT",EDGE,{"derivedFrom":sQuery(id+"F3.wireOp",EDGE,"E63")}),1.0]])]});
            extrude(context, id + "F14", {"entities" : qUnion([Q0]), "operationType" : NewBodyOperationType.REMOVE, "oppositeDirection" : true, "depth" : 25 * mm});
        }
        {
            var Q0;
            Q0=makeQuery(id+"F5.opExtrude","CAP_FACE",FACE,{"disambiguationData":[OSD([sQuery(id+"F0.wireOp",EDGE,"E0")])],"isStart":false});
            var sketch = newSketch(context, id + "F15", { "sketchPlane" : qUnion([Q0])});
            skLineSegment(sketch, "E125", {"start": v(42.08, 2) * mm, "end": v(39.6, 5.09) * mm});
            skLineSegment(sketch, "E126", {"start": v(39.6, 5.09) * mm, "end": v(40.56, 9.07) * mm});
            skLineSegment(sketch, "E127", {"start": v(40.56, 9.07) * mm, "end": v(38.19, 11.4) * mm});
            skLineSegment(sketch, "E128", {"start": v(38.19, 11.4) * mm, "end": v(14.32, 2.68) * mm});
            skLineSegment(sketch, "E129", {"start": v(14.32, 2.68) * mm, "end": v(13.6, 0.67) * mm});
            skLineSegment(sketch, "E130", {"start": v(13.6, 0.67) * mm, "end": v(17.37, -4.63) * mm});
            skLineSegment(sketch, "E131", {"start": v(17.37, -4.63) * mm, "end": v(28.02, -3.3) * mm});
            skLineSegment(sketch, "E132", {"start": v(28.02, -3.3) * mm, "end": v(33.24, 0.5) * mm});
            skLineSegment(sketch, "E133", {"start": v(33.24, 0.5) * mm, "end": v(42.08, 2) * mm});
            skSolve(sketch);
        }
        {
            var Q0;
            Q0=makeQuery(id+"F15.imprint","IMPRINT",FACE,{"disambiguationData":[TD([[makeQuery(id+"F15.imprint","IMPRINT",EDGE,{"derivedFrom":sQuery(id+"F15.wireOp",EDGE,"E125")}),1.0]])]});
            extrude(context, id + "F16", {"entities" : qUnion([Q0]), "operationType" : NewBodyOperationType.REMOVE, "oppositeDirection" : true, "depth" : 25 * mm});
        }
        {
            var Q0;
            Q0=makeQuery(id+"F5.opExtrude","CAP_FACE",FACE,{"disambiguationData":[OSD([sQuery(id+"F0.wireOp",EDGE,"E0")])],"isStart":false});
            var sketch = newSketch(context, id + "F17", { "sketchPlane" : qUnion([Q0])});
            skLineSegment(sketch, "E134", {"start": v(35.7, -18.66) * mm, "end": v(36.18, -13.72) * mm});
            skLineSegment(sketch, "E135", {"start": v(36.18, -13.72) * mm, "end": v(24.16, -10.3) * mm});
            skLineSegment(sketch, "E136", {"start": v(24.16, -10.3) * mm, "end": v(19.58, -11.06) * mm});
            skLineSegment(sketch, "E137", {"start": v(19.58, -11.06) * mm, "end": v(20.5, -19.34) * mm});
            skLineSegment(sketch, "E138", {"start": v(20.5, -19.34) * mm, "end": v(35.7, -18.66) * mm});
            skLineSegment(sketch, "E139", {"start": v(33.77, -20.7) * mm, "end": v(20.79, -20.7) * mm});
            skLineSegment(sketch, "E140", {"start": v(20.79, -20.7) * mm, "end": v(22.16, -28.1) * mm});
            skLineSegment(sketch, "E141", {"start": v(22.16, -28.1) * mm, "end": v(24.2, -33.56) * mm});
            skLineSegment(sketch, "E142", {"start": v(24.2, -33.56) * mm, "end": v(24.24, -39.6) * mm});
            skLineSegment(sketch, "E143", {"start": v(24.24, -39.6) * mm, "end": v(23.4, -41.56) * mm});
            skLineSegment(sketch, "E144", {"start": v(23.4, -41.56) * mm, "end": v(34.9, -41.56) * mm});
            skLineSegment(sketch, "E145", {"start": v(34.9, -41.56) * mm, "end": v(39.15, -36.13) * mm});
            skLineSegment(sketch, "E146", {"start": v(39.15, -36.13) * mm, "end": v(39.75, -32.28) * mm});
            skLineSegment(sketch, "E147", {"start": v(39.75, -32.28) * mm, "end": v(40.2, -31.27) * mm});
            skLineSegment(sketch, "E148", {"start": v(40.2, -31.27) * mm, "end": v(42.12, -29.87) * mm});
            skLineSegment(sketch, "E149", {"start": v(42.12, -29.87) * mm, "end": v(42.12, -27.9) * mm});
            skLineSegment(sketch, "E150", {"start": v(42.12, -27.9) * mm, "end": v(38.23, -27.54) * mm});
            skLineSegment(sketch, "E151", {"start": v(38.23, -27.54) * mm, "end": v(34.97, -26.33) * mm});
            skLineSegment(sketch, "E152", {"start": v(34.97, -26.33) * mm, "end": v(32.64, -23.84) * mm});
            skLineSegment(sketch, "E153", {"start": v(32.64, -23.84) * mm, "end": v(32.64, -21.87) * mm});
            skLineSegment(sketch, "E154", {"start": v(32.64, -21.87) * mm, "end": v(33.77, -20.7) * mm});
            skLineSegment(sketch, "E155", {"start": v(43.05, -21.91) * mm, "end": v(41.12, -20.02) * mm});
            skLineSegment(sketch, "E156", {"start": v(41.12, -20.02) * mm, "end": v(38.23, -20.02) * mm});
            skLineSegment(sketch, "E157", {"start": v(38.23, -20.02) * mm, "end": v(39.2, -12.71) * mm});
            skLineSegment(sketch, "E158", {"start": v(39.2, -12.71) * mm, "end": v(47.44, -13.8) * mm});
            skLineSegment(sketch, "E159", {"start": v(47.44, -13.8) * mm, "end": v(43.05, -21.91) * mm});
            skLineSegment(sketch, "E160", {"start": v(48.31, -11.47) * mm, "end": v(48.31, -8.53) * mm});
            skLineSegment(sketch, "E161", {"start": v(48.31, -8.53) * mm, "end": v(46.9, -7.17) * mm});
            skLineSegment(sketch, "E162", {"start": v(46.9, -7.17) * mm, "end": v(42.69, -8.7) * mm});
            skLineSegment(sketch, "E163", {"start": v(42.69, -8.7) * mm, "end": v(41.68, -9.22) * mm});
            skLineSegment(sketch, "E164", {"start": v(41.68, -9.22) * mm, "end": v(40.28, -8.37) * mm});
            skLineSegment(sketch, "E165", {"start": v(40.28, -8.37) * mm, "end": v(39.11, -8.45) * mm});
            skLineSegment(sketch, "E166", {"start": v(39.11, -8.45) * mm, "end": v(39.26, -10.68) * mm});
            skLineSegment(sketch, "E167", {"start": v(39.26, -10.68) * mm, "end": v(48.31, -11.47) * mm});
            skLineSegment(sketch, "E168", {"start": v(34.57, -4.92) * mm, "end": v(37.06, -1.46) * mm});
            skLineSegment(sketch, "E169", {"start": v(37.06, -1.46) * mm, "end": v(38.67, -1.78) * mm});
            skLineSegment(sketch, "E170", {"start": v(38.67, -1.78) * mm, "end": v(43.29, -1.78) * mm});
            skLineSegment(sketch, "E171", {"start": v(43.29, -1.78) * mm, "end": v(43.33, -3.87) * mm});
            skLineSegment(sketch, "E172", {"start": v(43.33, -3.87) * mm, "end": v(41.72, -5.12) * mm});
            skLineSegment(sketch, "E173", {"start": v(41.72, -5.12) * mm, "end": v(39.95, -5.04) * mm});
            skLineSegment(sketch, "E174", {"start": v(39.95, -5.04) * mm, "end": v(37.62, -6.4) * mm});
            skLineSegment(sketch, "E175", {"start": v(37.62, -6.4) * mm, "end": v(34.57, -4.92) * mm});
            skLineSegment(sketch, "E176", {"start": v(33.77, -5.6) * mm, "end": v(29.9, -5.6) * mm});
            skLineSegment(sketch, "E177", {"start": v(29.9, -5.6) * mm, "end": v(36.34, -12.63) * mm});
            skLineSegment(sketch, "E178", {"start": v(36.34, -12.63) * mm, "end": v(36.82, -9.98) * mm});
            skLineSegment(sketch, "E179", {"start": v(36.82, -9.98) * mm, "end": v(33.77, -5.6) * mm});
            skLineSegment(sketch, "E180", {"start": v(23.76, -8.97) * mm, "end": v(23.76, -7.37) * mm});
            skLineSegment(sketch, "E181", {"start": v(23.76, -7.37) * mm, "end": v(24.45, -6.16) * mm});
            skLineSegment(sketch, "E182", {"start": v(24.45, -6.16) * mm, "end": v(18.26, -6.16) * mm});
            skLineSegment(sketch, "E183", {"start": v(18.26, -6.16) * mm, "end": v(19.3, -9.66) * mm});
            skLineSegment(sketch, "E184", {"start": v(19.3, -9.66) * mm, "end": v(23.76, -8.97) * mm});
            skSolve(sketch);
        }
        {
            var Q0;
            Q0=makeQuery(id+"F17.imprint","IMPRINT",FACE,{"disambiguationData":[TD([[makeQuery(id+"F17.imprint","IMPRINT",EDGE,{"derivedFrom":sQuery(id+"F17.wireOp",EDGE,"E139")}),1.0]])]});
            var Q1;
            Q1=makeQuery(id+"F17.imprint","IMPRINT",FACE,{"disambiguationData":[TD([[makeQuery(id+"F17.imprint","IMPRINT",EDGE,{"derivedFrom":sQuery(id+"F17.wireOp",EDGE,"E134")}),1.0]])]});
            var Q2;
            Q2=makeQuery(id+"F17.imprint","IMPRINT",FACE,{"disambiguationData":[TD([[makeQuery(id+"F17.imprint","IMPRINT",EDGE,{"derivedFrom":sQuery(id+"F17.wireOp",EDGE,"E176")}),1.0]])]});
            var Q3;
            Q3=makeQuery(id+"F17.imprint","IMPRINT",FACE,{"disambiguationData":[TD([[makeQuery(id+"F17.imprint","IMPRINT",EDGE,{"derivedFrom":sQuery(id+"F17.wireOp",EDGE,"E155")}),-1.0]])]});
            var Q4;
            Q4=makeQuery(id+"F17.imprint","IMPRINT",FACE,{"disambiguationData":[TD([[makeQuery(id+"F17.imprint","IMPRINT",EDGE,{"derivedFrom":sQuery(id+"F17.wireOp",EDGE,"E160")}),1.0]])]});
            var Q5;
            Q5=makeQuery(id+"F17.imprint","IMPRINT",FACE,{"disambiguationData":[TD([[makeQuery(id+"F17.imprint","IMPRINT",EDGE,{"derivedFrom":sQuery(id+"F17.wireOp",EDGE,"E180")}),1.0]])]});
            var Q6;
            Q6=makeQuery(id+"F17.imprint","IMPRINT",FACE,{"disambiguationData":[TD([[makeQuery(id+"F17.imprint","IMPRINT",EDGE,{"derivedFrom":sQuery(id+"F17.wireOp",EDGE,"E168")}),-1.0]])]});
            extrude(context, id + "F18", {"entities" : qUnion([Q0, Q1, Q2, Q3, Q4, Q5, Q6]), "operationType" : NewBodyOperationType.REMOVE, "oppositeDirection" : true, "depth" : 25 * mm});
        }
    });
